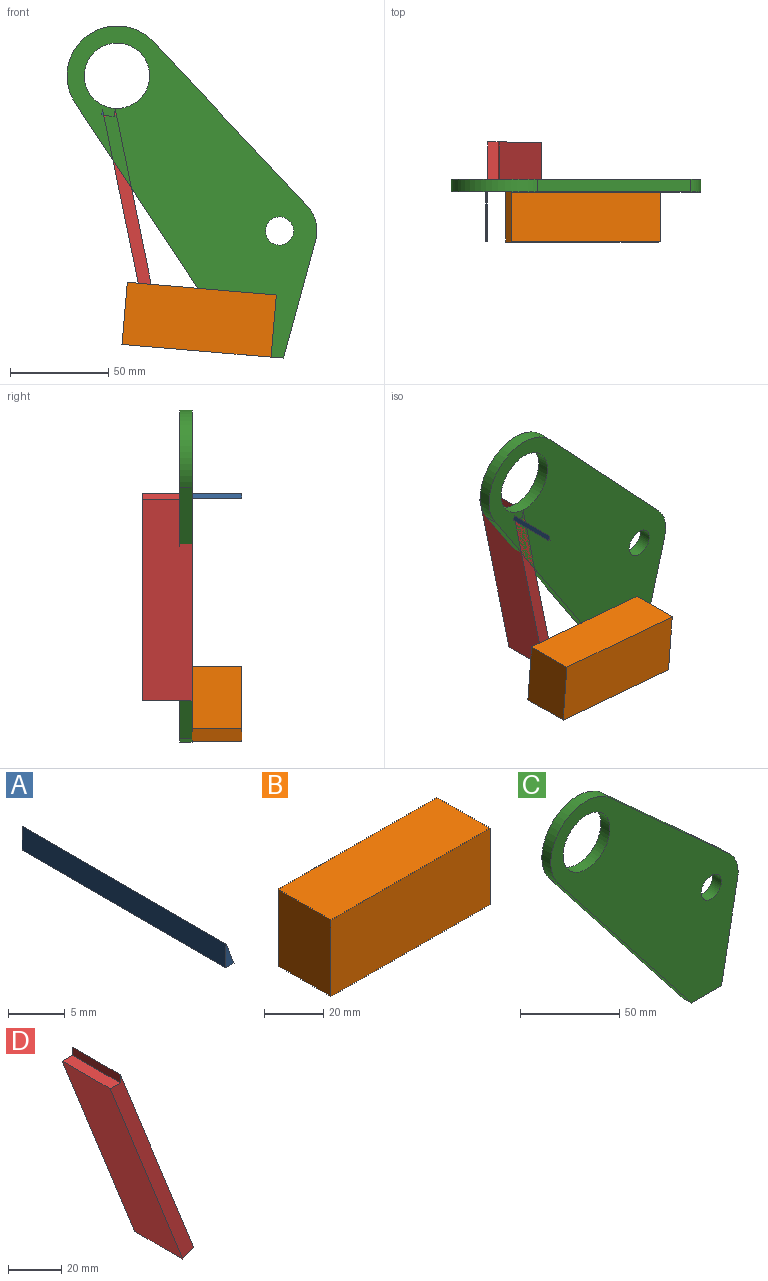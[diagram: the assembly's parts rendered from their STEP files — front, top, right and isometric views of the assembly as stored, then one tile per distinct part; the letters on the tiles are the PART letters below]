
ASSEMBLY  parts=4 mates=4
PART A: 5 faces, bbox 1x25.4x2.6 mm
  f0: plane 25.4x2.57mm, normal (0.93,0,0.37), area 70.2mm2, adj f1,f2,f3,f4
  f1: plane 25.4x2.57mm, normal (-1,0,0), area 65.3mm2, adj f0,f2,f3,f4
  f2: plane 25.4x1.01mm, normal (0,0,-1), area 25.8mm2, adj f0,f1,f3,f4
  f3: plane 2.57x1.01mm, normal (0,-1,0), area 1.3mm2, adj f0,f1,f2
  f4: plane 2.57x1.01mm, normal (0,1,0), area 1.3mm2, adj f0,f1,f2
PART B: 6 faces, bbox 76.2x25.4x31.8 mm
  f0: plane 76.2x25.4mm, normal (0,0,1), area 1935.5mm2, adj f1,f3,f4,f5
  f1: plane 31.75x25.4mm, normal (-1,0,0), area 806.5mm2, adj f0,f2,f4,f5
  f2: plane 76.2x25.4mm, normal (0,0,-1), area 1935.5mm2, adj f1,f3,f4,f5
  f3: plane 31.75x25.4mm, normal (1,0,0), area 806.5mm2, adj f0,f2,f4,f5
  f4: plane 76.2x31.75mm, normal (0,-1,0), area 2419.3mm2, adj f0,f1,f2,f3
  f5: plane 76.2x31.75mm, normal (0,1,0), area 2419.3mm2, adj f0,f1,f2,f3
PART C: 10 faces, bbox 133.4x6.4x161.9 mm
  f0: plane 120.86x94.72mm, normal (-0.79,0,-0.62), area 975.1mm2, adj f1,f5,f8,f9
  f1: plane 21.44x6.35mm, normal (0,0,-1), area 136.1mm2, adj f0,f2,f8,f9
  f2: plane 60.81x11.45mm, normal (0.98,0,-0.19), area 392.9mm2, adj f1,f3,f8,f9
  f3: cylinder r=19.05mm len=17.63mm, axis (0,-1,0), area 123.3mm2, adj f2,f4,f8,f9
  f4: plane 84.63x76.89mm, normal (0.67,0,0.74), area 726.1mm2, adj f3,f5,f8,f9
  f5: cylinder r=25.4mm len=42.48mm, axis (0,-1,0), area 479.5mm2, adj f0,f4,f8,f9
  f6: cylinder r=7.19mm len=14.38mm, axis (0,-1,0), area 286.8mm2, adj f8,f9
  f7: cylinder r=16.67mm len=33.34mm, axis (0,-1,0), area 665.1mm2, adj f8,f9
  f8: plane 161.93x133.35mm, normal (0,1,0), area 9250.6mm2, adj f0,f1,f2,f3,f4,f5,f6,f7
  f9: plane 161.93x133.35mm, normal (0,-1,0), area 9250.6mm2, adj f0,f1,f2,f3,f4,f5,f6,f7
PART D: 7 faces, bbox 44.4x25.4x101.3 mm
  f0: plane 97.51x38.47mm, normal (-0.93,0,-0.37), area 2662.7mm2, adj f1,f4,f5,f6
  f1: plane 25.4x5.91mm, normal (0.37,0,-0.93), area 161.3mm2, adj f0,f2,f5,f6
  f2: plane 98.96x39.04mm, normal (0.93,0,0.37), area 2702.2mm2, adj f1,f3,f5,f6
  f3: plane 25.4x3.78mm, normal (-1,0,0), area 96mm2, adj f2,f4,f5,f6
  f4: plane 25.4x5.34mm, normal (0,0,1), area 135.5mm2, adj f0,f3,f5,f6
  f5: plane 101.29x44.38mm, normal (0,1,0), area 660.5mm2, adj f0,f1,f2,f3,f4
  f6: plane 101.29x44.38mm, normal (0,-1,0), area 660.5mm2, adj f0,f1,f2,f3,f4
PLACE A rot(axis=(0,1,0),13.2deg) t=(0,0,0)mm fixed
PLACE B rot(axis=(0,1,0),4.9deg) t=(-11.39,0,-1.82)mm
PLACE C rot(axis=(0,1,0),4.6deg) t=(-10.93,0,-136.09)mm
PLACE D rot(axis=(0,1,0),9.9deg) t=(-1,0,0.2)mm
MATE revolute B.f5 <-> D.f6  axis (0,-1,0) through (16.85,0,-118.95)mm
MATE revolute C.f9 <-> B.f5  axis (0,-1,0) through (67.46,0,-123.27)mm
MATE revolute A.f4 <-> D.f6  axis (0,-1,0) through (-4.05,0,-17.26)mm
MATE revolute A.f4 <-> C.f5  axis (0,-1,0) through (0,0,0)mm
